# Revit family: 17_0620_ergoCentric_tCentric Hybrid
name_source: partatom
category: Furniture
revit_build: Autodesk Revit 2016 (Build: 20150714_1515(x64)
units: mm (PartAtom-declared; Revit-internal decimal feet)

## family parameters
Always vertical = Yes
Cut with Voids When Loaded = No
Room Calculation Point = No
Shared = No
Work Plane-Based = No

## types (1)
- 17_0620_ergoCentric_tCentric Hybrid
    Back Upholstery = Steelcase - BR09 Sterling Blue (3D Knit)
    Description = The tCentric Hybrid provides comfort and safety without compromising on style. Featuring a dual curve backrest that adjusts vertically to ensure lumbar support remains in alignment with the frame’s lumbar curve, the tCentric Hybrid offers a minimalist design that will satisfy even the most demanding users.
    Manufacturer = ergoCentric
    Material = Leather_Black
    MaterialBase = Metal Black
    Model = tCentric Hybrid
    Top = <By Category>
    URL = https://www.ergocentric.com
    armSupporter = armSupporter
    timber = <By Category>

## geometry (parser evidence)
native form markers: Blend x4, Sweep x47
no freeform markers — native parametric forms only
